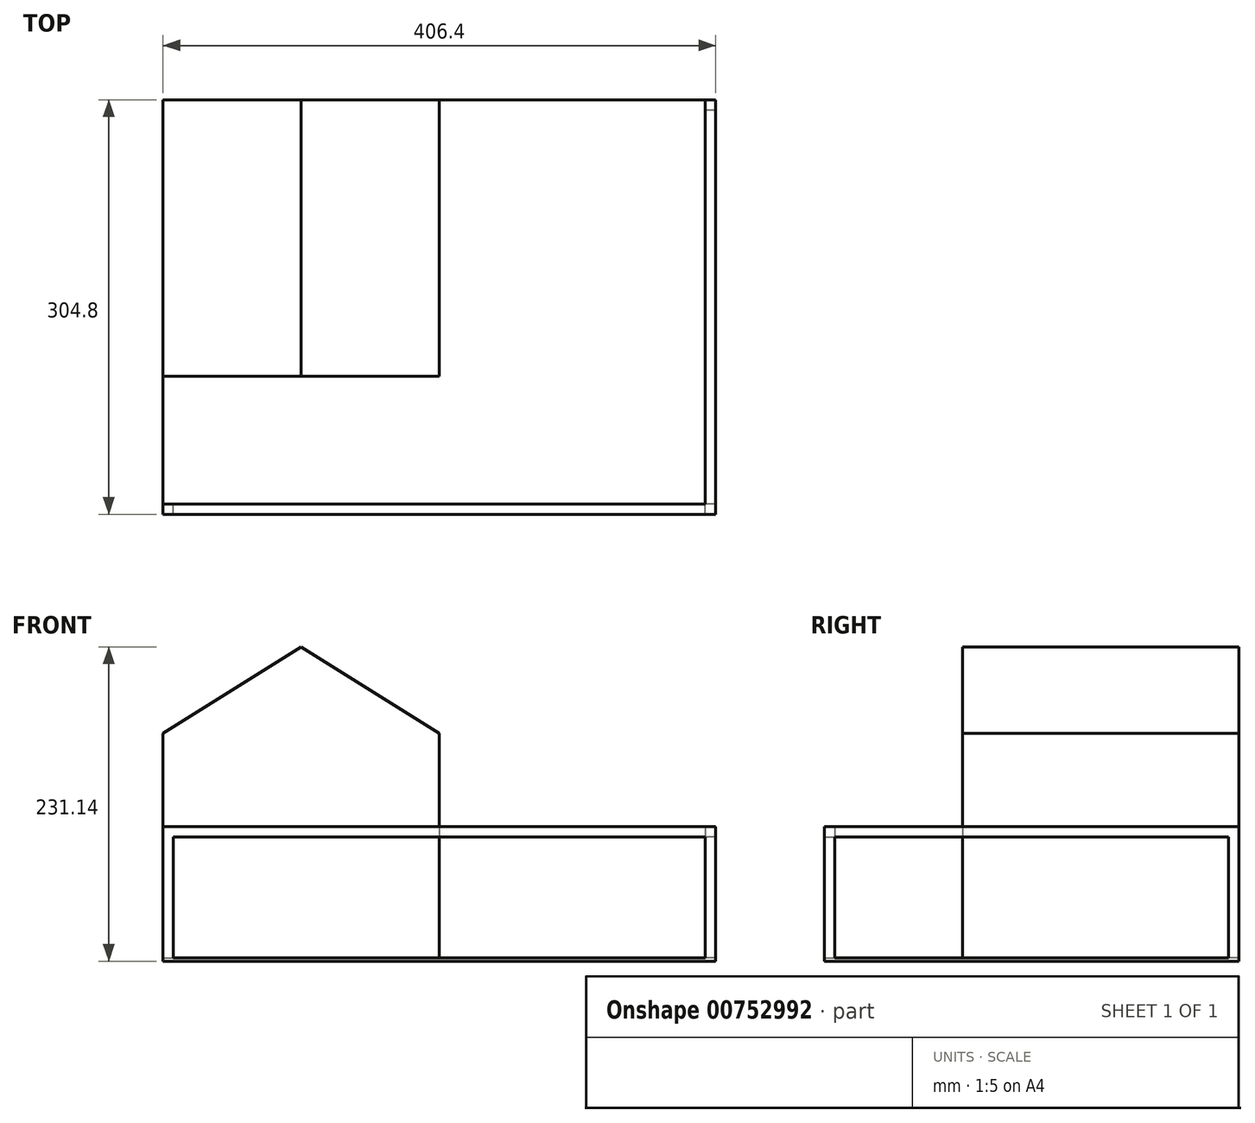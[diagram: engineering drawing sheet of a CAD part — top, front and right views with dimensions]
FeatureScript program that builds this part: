
annotation { "Feature Type Name" : "Feature", "Feature Type Description" : "" }
export const myFeature = defineFeature(function(context is Context, id is Id, definition is map)
    precondition{}
    {
        {
            var Q0;
            Q0=qCreatedBy(makeId("Top.planeOp"),FACE);
            var sketch = newSketch(context, id + "F0", { "sketchPlane" : qUnion([Q0])});
            skLineSegment(sketch, "E0.bottom", {"start": v(-393.3, 267.53) * mm, "end": v(13.1, 267.53) * mm});
            skLineSegment(sketch, "E0.top", {"start": v(-393.3, -37.27) * mm, "end": v(13.1, -37.27) * mm});
            skLineSegment(sketch, "E0.left", {"start": v(-393.3, 267.53) * mm, "end": v(-393.3, -37.27) * mm});
            skLineSegment(sketch, "E0.right", {"start": v(13.1, 267.53) * mm, "end": v(13.1, -37.27) * mm});
            skSolve(sketch);
        }
        {
            var Q0;
            Q0 = qSketchRegion(id + "F0", true);
            extrude(context, id + "F1", {"entities" : qUnion([Q0]), "depth" : 2.54 * mm, "offsetDistance" : 25.4 * mm});
        }
        {
            var Q0;
            Q0=makeQuery(id+"F1.opExtrude","CAP_FACE",FACE,{"disambiguationData":[OSD([sQuery(id+"F0.wireOp",EDGE,"E0.bottom"),sQuery(id+"F0.wireOp",EDGE,"E0.top"),sQuery(id+"F0.wireOp",EDGE,"E0.left"),sQuery(id+"F0.wireOp",EDGE,"E0.right")])],"isStart":false});
            var sketch = newSketch(context, id + "F2", { "sketchPlane" : qUnion([Q0])});
            skLineSegment(sketch, "E1.bottom", {"start": v(-393.3, -37.27) * mm, "end": v(-385.68, -37.27) * mm});
            skLineSegment(sketch, "E1.left", {"start": v(-393.3, -37.27) * mm, "end": v(-393.3, -25.63) * mm});
            skLineSegment(sketch, "E2.bottom", {"start": v(13.1, -37.27) * mm, "end": v(5.48, -37.27) * mm});
            skLineSegment(sketch, "E2.left", {"start": v(13.1, -37.27) * mm, "end": v(13.1, -27.18) * mm});
            skLineSegment(sketch, "E3.bottom", {"start": v(13.1, 267.53) * mm, "end": v(5.48, 267.53) * mm});
            skLineSegment(sketch, "E3.top", {"start": v(13.1, 259.9) * mm, "end": v(5.48, 259.9) * mm});
            skLineSegment(sketch, "E3.left", {"start": v(13.1, 267.53) * mm, "end": v(13.1, 259.9) * mm});
            skLineSegment(sketch, "E3.right", {"start": v(5.48, 267.53) * mm, "end": v(5.48, 259.9) * mm});
            skLineSegment(sketch, "E4.top", {"start": v(13.1, -29.65) * mm, "end": v(5.48, -29.65) * mm});
            skLineSegment(sketch, "E4.left", {"start": v(13.1, -37.27) * mm, "end": v(13.1, -29.65) * mm});
            skLineSegment(sketch, "E4.right", {"start": v(5.48, -37.27) * mm, "end": v(5.48, -29.65) * mm});
            skLineSegment(sketch, "E5.bottom", {"start": v(-385.68, -37.27) * mm, "end": v(-393.3, -37.27) * mm});
            skLineSegment(sketch, "E5.top", {"start": v(-385.68, -29.65) * mm, "end": v(-393.3, -29.65) * mm});
            skLineSegment(sketch, "E5.left", {"start": v(-385.68, -37.27) * mm, "end": v(-385.68, -29.65) * mm});
            skLineSegment(sketch, "E5.right", {"start": v(-393.3, -37.27) * mm, "end": v(-393.3, -29.65) * mm});
            skSolve(sketch);
        }
        {
            var Q0;
            Q0 = qSketchRegion(id + "F2", true);
            extrude(context, id + "F3", {"entities" : qUnion([Q0]), "operationType" : NewBodyOperationType.ADD, "depth" : 88.9 * mm, "offsetDistance" : 25.4 * mm});
        }
        {
            var Q0;
            Q0=makeQuery(id+"F1.opExtrude","CAP_FACE",FACE,{"disambiguationData":[OSD([sQuery(id+"F0.wireOp",EDGE,"E0.bottom"),sQuery(id+"F0.wireOp",EDGE,"E0.top"),sQuery(id+"F0.wireOp",EDGE,"E0.left"),sQuery(id+"F0.wireOp",EDGE,"E0.right")])],"isStart":false});
            var sketch = newSketch(context, id + "F4", { "sketchPlane" : qUnion([Q0])});
            skLineSegment(sketch, "E6.bottom", {"start": v(-393.3, 267.53) * mm, "end": v(-190.1, 267.53) * mm});
            skLineSegment(sketch, "E6.top", {"start": v(-393.3, 64.33) * mm, "end": v(-190.1, 64.33) * mm});
            skLineSegment(sketch, "E6.left", {"start": v(-393.3, 267.53) * mm, "end": v(-393.3, 64.33) * mm});
            skLineSegment(sketch, "E6.right", {"start": v(-190.1, 267.53) * mm, "end": v(-190.1, 64.33) * mm});
            skSolve(sketch);
        }
        {
            var Q0;
            Q0 = qSketchRegion(id + "F4", true);
            extrude(context, id + "F5", {"entities" : qUnion([Q0]), "operationType" : NewBodyOperationType.ADD, "depth" : 165.1 * mm, "offsetDistance" : 25.4 * mm});
        }
        {
            var Q0;
            Q0=makeQuery(id+"F5.opExtrude","SWEPT_FACE",FACE,{"disambiguationData":[OSD([sQuery(id+"F4.wireOp",EDGE,"E6.top")])]});
            var sketch = newSketch(context, id + "F6", { "sketchPlane" : qUnion([Q0])});
            skLineSegment(sketch, "E7", {"start": v(-393.3, 167.64) * mm, "end": v(-291.7, 167.64) * mm});
            skLineSegment(sketch, "E8", {"start": v(-291.7, 167.64) * mm, "end": v(-291.7, 231.14) * mm});
            skLineSegment(sketch, "E9", {"start": v(-291.7, 231.14) * mm, "end": v(-393.3, 167.64) * mm});
            skLineSegment(sketch, "E10", {"start": v(-291.7, 231.14) * mm, "end": v(-190.1, 167.64) * mm});
            skLineSegment(sketch, "E11", {"start": v(-291.7, 167.64) * mm, "end": v(-190.1, 167.64) * mm});
            skSolve(sketch);
        }
        {
            var Q0;
            Q0 = qSketchRegion(id + "F6", true);
            extrude(context, id + "F7", {"entities" : qUnion([Q0]), "operationType" : NewBodyOperationType.ADD, "oppositeDirection" : true, "depth" : 203.2 * mm, "offsetDistance" : 25.4 * mm});
        }
        {
            var Q0;
            Q0=makeQuery(id+"F3.opExtrude","CAP_FACE",FACE,{"disambiguationData":[OSD([sQuery(id+"F2.wireOp",EDGE,"E2.bottom"),sQuery(id+"F2.wireOp",EDGE,"E4.top"),sQuery(id+"F2.wireOp",EDGE,"E4.left"),sQuery(id+"F2.wireOp",EDGE,"E4.right")])],"isStart":false});
            var sketch = newSketch(context, id + "F8", { "sketchPlane" : qUnion([Q0])});
            skLineSegment(sketch, "E12.bottom", {"start": v(13.1, -37.27) * mm, "end": v(-393.3, -37.27) * mm});
            skLineSegment(sketch, "E12.top", {"start": v(13.1, -29.65) * mm, "end": v(-393.3, -29.65) * mm});
            skLineSegment(sketch, "E12.left", {"start": v(13.1, -37.27) * mm, "end": v(13.1, -29.65) * mm});
            skLineSegment(sketch, "E12.right", {"start": v(-393.3, -37.27) * mm, "end": v(-393.3, -29.65) * mm});
            skLineSegment(sketch, "E13.bottom", {"start": v(5.48, -29.65) * mm, "end": v(13.1, -29.65) * mm});
            skLineSegment(sketch, "E13.top", {"start": v(5.48, 267.53) * mm, "end": v(13.1, 267.53) * mm});
            skLineSegment(sketch, "E13.left", {"start": v(5.48, -29.65) * mm, "end": v(5.48, 267.53) * mm});
            skLineSegment(sketch, "E13.right", {"start": v(13.1, -29.65) * mm, "end": v(13.1, 267.53) * mm});
            skSolve(sketch);
        }
        {
            var Q0;
            Q0 = qSketchRegion(id + "F8", true);
            extrude(context, id + "F9", {"entities" : qUnion([Q0]), "operationType" : NewBodyOperationType.ADD, "depth" : 7.62 * mm, "offsetDistance" : 25.4 * mm});
        }
    });
